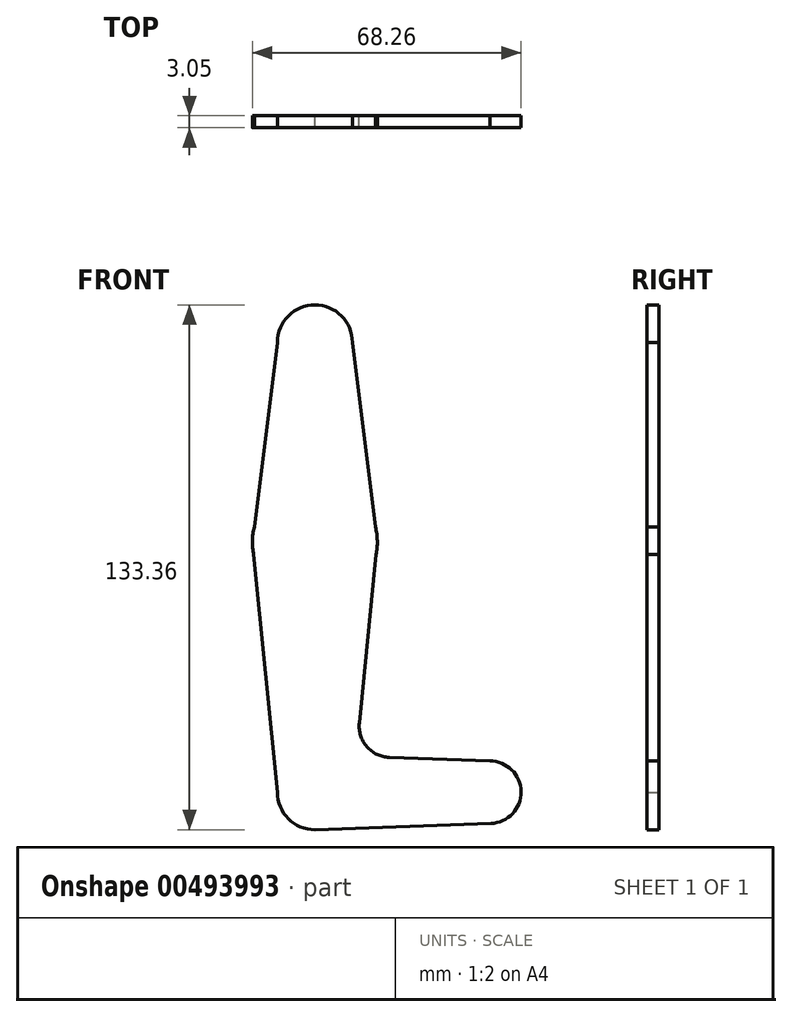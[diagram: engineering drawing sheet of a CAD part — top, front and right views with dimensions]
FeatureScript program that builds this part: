
annotation { "Feature Type Name" : "Feature", "Feature Type Description" : "" }
export const myFeature = defineFeature(function(context is Context, id is Id, definition is map)
    precondition{}
    {
        {
            var Q0;
            Q0=qCreatedBy(makeId("Front.planeOp"),FACE);
            var sketch = newSketch(context, id + "F0", { "sketchPlane" : qUnion([Q0])});
            skLineSegment(sketch, "E0", {"start": v(0, 0) * mm, "end": v(0, 114.3) * mm, "construction": true});
            skLineSegment(sketch, "E1", {"start": v(0, 0) * mm, "end": v(44.45, 0) * mm, "construction": true});
            skCircle(sketch, "E2", {"center": v(0, 114.3) * mm, "radius": 9.52 * mm});
            skCircle(sketch, "E3", {"center": v(0, 63.5) * mm, "radius": 15.88 * mm});
            skCircle(sketch, "E4", {"center": v(0, 0) * mm, "radius": 9.53 * mm});
            skCircle(sketch, "E5", {"center": v(44.45, 0) * mm, "radius": 7.94 * mm});
            skLineSegment(sketch, "E6", {"start": v(-15.88, 63.5) * mm, "end": v(-9.52, 114.3) * mm});
            skLineSegment(sketch, "E7", {"start": v(15.88, 63.5) * mm, "end": v(9.52, 114.3) * mm});
            skLineSegment(sketch, "E8", {"start": v(-15.88, 63.5) * mm, "end": v(-9.52, 0) * mm});
            skLineSegment(sketch, "E9", {"start": v(15.88, 63.5) * mm, "end": v(11.28, 17.59) * mm});
            skLineSegment(sketch, "E10", {"start": v(18.91, 8.85) * mm, "end": v(44.45, 7.94) * mm});
            skLineSegment(sketch, "E11", {"start": v(0, -9.52) * mm, "end": v(44.73, -7.93) * mm});
            skCircle(sketch, "E12", {"center": v(0, 114.3) * mm, "radius": 4.25 * mm});
            skCircle(sketch, "E13", {"center": v(0, 63.5) * mm, "radius": 5.18 * mm});
            skCircle(sketch, "E14", {"center": v(0, 0) * mm, "radius": 3.89 * mm});
            skCircle(sketch, "E15", {"center": v(44.45, 0) * mm, "radius": 3.23 * mm});
            skCircle(sketch, "E16", {"center": v(-3.6, 95.62) * mm, "radius": 3.18 * mm});
            skArc(sketch, "E17.filletArc", {"start": v(11.28, 17.59) * mm, "mid": v(13.2, 11.57) * mm, "end": v(18.91, 8.85) * mm});
            skSolve(sketch);
        }
        {
            var Q0;
            Q0=makeQuery(id+"F0.imprint","IMPRINT",FACE,{"disambiguationData":[TD([[makeQuery(id+"F0.imprint","IMPRINT",EDGE,{"derivedFrom":sQuery(id+"F0.wireOp",EDGE,"E13")}),-1.0]])]});
            var Q1;
            {var subQ8=sQuery(id+"F0.wireOp",EDGE,"E10");Q1=makeQuery(id+"F0.imprint","IMPRINT",FACE,{"disambiguationData":[TD([[makeQuery(id+"F0.imprint","IMPRINT",EDGE,{"derivedFrom":subQ8}),-1.0]])]});}
            var Q2;
            Q2=makeQuery(id+"F0.imprint","IMPRINT",FACE,{"disambiguationData":[TD([[makeQuery(id+"F0.imprint","IMPRINT",EDGE,{"derivedFrom":sQuery(id+"F0.wireOp",EDGE,"E14")}),-1.0]])]});
            var Q3;
            Q3=makeQuery(id+"F0.imprint","IMPRINT",FACE,{"disambiguationData":[TD([[makeQuery(id+"F0.imprint","IMPRINT",EDGE,{"derivedFrom":sQuery(id+"F0.wireOp",EDGE,"E13")}),1.0]])]});
            var Q4;
            Q4=makeQuery(id+"F0.imprint","IMPRINT",FACE,{"disambiguationData":[TD([[makeQuery(id+"F0.imprint","IMPRINT",EDGE,{"derivedFrom":sQuery(id+"F0.wireOp",EDGE,"E12")}),-1.0]])]});
            var Q5;
            Q5=makeQuery(id+"F0.imprint","IMPRINT",FACE,{"disambiguationData":[TD([[makeQuery(id+"F0.imprint","IMPRINT",EDGE,{"derivedFrom":sQuery(id+"F0.wireOp",EDGE,"E15")}),-1.0]])]});
            var Q6;
            Q6=makeQuery(id+"F0.imprint","IMPRINT",FACE,{"disambiguationData":[TD([[makeQuery(id+"F0.imprint","IMPRINT",EDGE,{"derivedFrom":sQuery(id+"F0.wireOp",EDGE,"E16")}),-1.0]])]});
            var Q7;
            {var subQ0=sQuery(id+"F0.wireOp",EDGE,"E7");var subQ1=sQuery(id+"F0.wireOp",EDGE,"E3");var subQ3=makeQuery(id+"F0.imprint","INTERSECT",VERTEX,{"derivedFrom":[subQ1,subQ0]});Q7=makeQuery(id+"F0.imprint","IMPRINT",FACE,{"disambiguationData":[TD([[makeQuery(id+"F0.imprint","IMPRINT",EDGE,{"disambiguationData":[TD([[subQ3,1.0]])],"derivedFrom":subQ1}),1.0]])]});}
            var Q8;
            {var subQ0=sQuery(id+"F0.wireOp",EDGE,"E6");var subQ1=sQuery(id+"F0.wireOp",EDGE,"E3");var subQ3=makeQuery(id+"F0.imprint","INTERSECT",VERTEX,{"derivedFrom":[subQ1,subQ0]});Q8=makeQuery(id+"F0.imprint","IMPRINT",FACE,{"disambiguationData":[TD([[makeQuery(id+"F0.imprint","IMPRINT",EDGE,{"disambiguationData":[TD([[subQ3,-1.0]])],"derivedFrom":subQ1}),1.0]])]});}
            var Q9;
            {var subQ0=sQuery(id+"F0.wireOp",EDGE,"E11");var subQ1=sQuery(id+"F0.wireOp",EDGE,"E4");var subQ2=makeQuery(id+"F0.imprint","INTERSECT",VERTEX,{"disambiguationData":[OD(0.0)],"derivedFrom":[subQ1,subQ0]});Q9=makeQuery(id+"F0.imprint","IMPRINT",FACE,{"disambiguationData":[TD([[makeQuery(id+"F0.imprint","IMPRINT",EDGE,{"disambiguationData":[TD([[subQ2,-1.0]])],"derivedFrom":subQ1}),1.0]])]});}
            var Q10;
            Q10=makeQuery(id+"F0.imprint","IMPRINT",FACE,{"disambiguationData":[TD([[makeQuery(id+"F0.imprint","IMPRINT",EDGE,{"derivedFrom":sQuery(id+"F0.wireOp",EDGE,"E12")}),1.0]])]});
            var Q11;
            Q11=makeQuery(id+"F0.imprint","IMPRINT",FACE,{"disambiguationData":[TD([[makeQuery(id+"F0.imprint","IMPRINT",EDGE,{"derivedFrom":sQuery(id+"F0.wireOp",EDGE,"E14")}),1.0]])]});
            var Q12;
            Q12=makeQuery(id+"F0.imprint","IMPRINT",FACE,{"disambiguationData":[TD([[makeQuery(id+"F0.imprint","IMPRINT",EDGE,{"derivedFrom":sQuery(id+"F0.wireOp",EDGE,"E15")}),1.0]])]});
            var Q13;
            Q13=makeQuery(id+"F0.imprint","IMPRINT",FACE,{"disambiguationData":[TD([[makeQuery(id+"F0.imprint","IMPRINT",EDGE,{"derivedFrom":sQuery(id+"F0.wireOp",EDGE,"E16")}),1.0]])]});
            var Q14;
            {var subQ0=sQuery(id+"F0.wireOp",EDGE,"E8");var subQ1=sQuery(id+"F0.wireOp",EDGE,"E3");var subQ3=makeQuery(id+"F0.imprint","INTERSECT",VERTEX,{"derivedFrom":[subQ1,subQ0]});Q14=makeQuery(id+"F0.imprint","IMPRINT",FACE,{"disambiguationData":[TD([[makeQuery(id+"F0.imprint","IMPRINT",EDGE,{"disambiguationData":[TD([[subQ3,1.0]])],"derivedFrom":subQ1}),1.0]])]});}
            var Q15;
            {var subQ0=sQuery(id+"F0.wireOp",EDGE,"E9");var subQ1=sQuery(id+"F0.wireOp",EDGE,"E3");var subQ3=makeQuery(id+"F0.imprint","INTERSECT",VERTEX,{"derivedFrom":[subQ1,subQ0]});Q15=makeQuery(id+"F0.imprint","IMPRINT",FACE,{"disambiguationData":[TD([[makeQuery(id+"F0.imprint","IMPRINT",EDGE,{"disambiguationData":[TD([[subQ3,-1.0]])],"derivedFrom":subQ1}),1.0]])]});}
            extrude(context, id + "F1", {"entities" : qUnion([Q0, Q1, Q2, Q3, Q4, Q5, Q6, Q7, Q8, Q9, Q10, Q11, Q12, Q13, Q14, Q15]), "depth" : 3.05 * mm});
        }
    });
